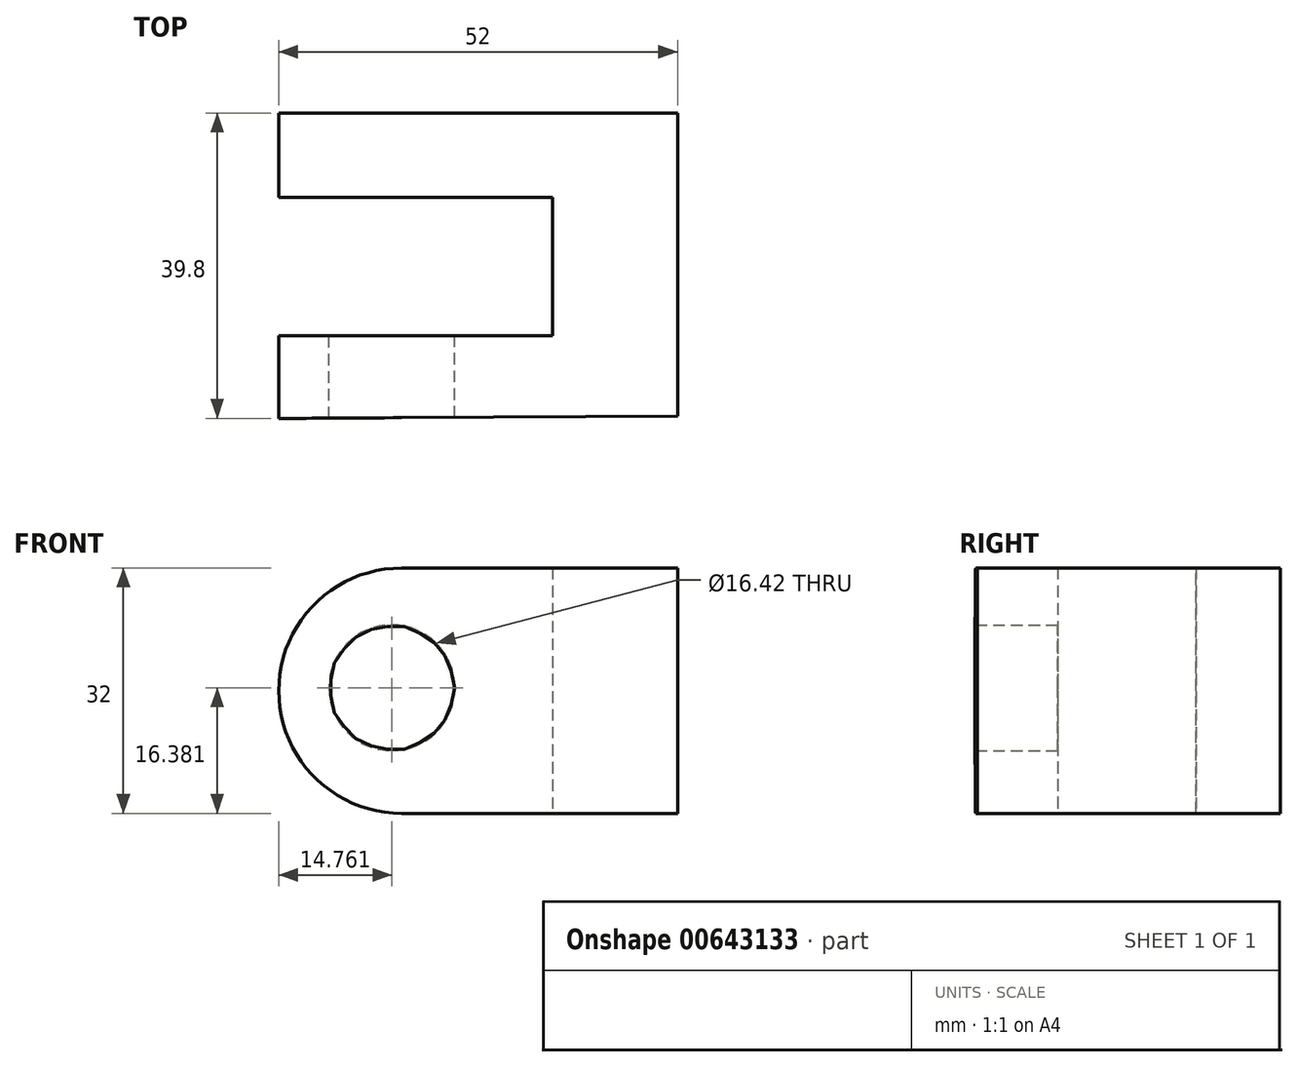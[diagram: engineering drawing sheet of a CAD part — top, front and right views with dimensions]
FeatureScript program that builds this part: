
annotation { "Feature Type Name" : "Feature", "Feature Type Description" : "" }
export const myFeature = defineFeature(function(context is Context, id is Id, definition is map)
    precondition{}
    {
        {
            var Q0;
            Q0=qCreatedBy(makeId("Top.planeOp"),FACE);
            var sketch = newSketch(context, id + "F0", { "sketchPlane" : qUnion([Q0])});
            skLineSegment(sketch, "E0", {"start": v(43.1, 25.26) * mm, "end": v(43.1, -14.24) * mm});
            skLineSegment(sketch, "E1", {"start": v(43.1, 25.26) * mm, "end": v(-8.9, 25.26) * mm});
            skLineSegment(sketch, "E2", {"start": v(-8.9, 25.26) * mm, "end": v(-8.9, 14.26) * mm});
            skLineSegment(sketch, "E3", {"start": v(-8.9, 14.26) * mm, "end": v(26.8, 14.26) * mm});
            skLineSegment(sketch, "E4", {"start": v(26.8, 14.26) * mm, "end": v(26.8, -3.74) * mm});
            skLineSegment(sketch, "E5", {"start": v(26.8, -3.74) * mm, "end": v(-8.9, -3.74) * mm});
            skLineSegment(sketch, "E6", {"start": v(-8.9, -3.74) * mm, "end": v(-8.9, -14.54) * mm});
            skLineSegment(sketch, "E7", {"start": v(-8.9, -14.54) * mm, "end": v(43.1, -14.24) * mm});
            skSolve(sketch);
        }
        {
            var Q0;
            Q0 = qSketchRegion(id + "F0", true);
            extrude(context, id + "F1", {"entities" : qUnion([Q0]), "depth" : 32 * mm, "offsetDistance" : 25 * mm});
        }
        {
            var Q0;
            Q0=makeQuery(id+"F1.opExtrude","CAP_EDGE",EDGE,{"disambiguationData":[OSD([sQuery(id+"F0.wireOp",EDGE,"E6")])],"isStart":false});
            fillet(context, id + "F2", {"entities" : qUnion([Q0]), "radius" : 16 * mm, "tangentPropagation" : true, "allowEdgeOverflow" : false});
        }
        {
            var Q0;
            Q0=makeQuery(id+"F1.opExtrude","CAP_EDGE",EDGE,{"disambiguationData":[OSD([sQuery(id+"F0.wireOp",EDGE,"E2")])],"isStart":false});
            fillet(context, id + "F3", {"entities" : qUnion([Q0]), "radius" : 16 * mm, "tangentPropagation" : true, "allowEdgeOverflow" : false});
        }
        {
            var Q0;
            Q0=makeQuery(id+"F1.opExtrude","CAP_EDGE",EDGE,{"disambiguationData":[OSD([sQuery(id+"F0.wireOp",EDGE,"E2")])],"isStart":true});
            fillet(context, id + "F4", {"entities" : qUnion([Q0]), "radius" : 16 * mm, "tangentPropagation" : true, "allowEdgeOverflow" : false});
        }
        {
            var Q0;
            Q0=makeQuery(id+"F1.opExtrude","CAP_EDGE",EDGE,{"disambiguationData":[OSD([sQuery(id+"F0.wireOp",EDGE,"E6")])],"isStart":true});
            fillet(context, id + "F5", {"entities" : qUnion([Q0]), "radius" : 16 * mm, "tangentPropagation" : true, "allowEdgeOverflow" : false});
        }
        {
            var Q0;
            Q0=qCreatedBy(makeId("Front.planeOp"),FACE);
            var sketch = newSketch(context, id + "F6", { "sketchPlane" : qUnion([Q0])});
            skCircle(sketch, "E8", {"center": v(5.86, 16.38) * mm, "radius": 8.2 * mm});
            skSolve(sketch);
        }
        {
            var Q0;
            Q0=makeQuery(id+"F6.imprint","IMPRINT",FACE,{"disambiguationData":[TD([[makeQuery(id+"F6.imprint","IMPRINT",EDGE,{"derivedFrom":sQuery(id+"F6.wireOp",EDGE,"E8")}),1.0]])]});
            var Q1;
            Q1=sQuery(id+"F6.wireOp",EDGE,"E8");
            extrude(context, id + "F7", {"entities" : qUnion([Q0]), "operationType" : NewBodyOperationType.REMOVE, "surfaceEntities" : qUnion([Q1]), "depth" : 16 * mm, "offsetDistance" : 25 * mm});
        }
    });
